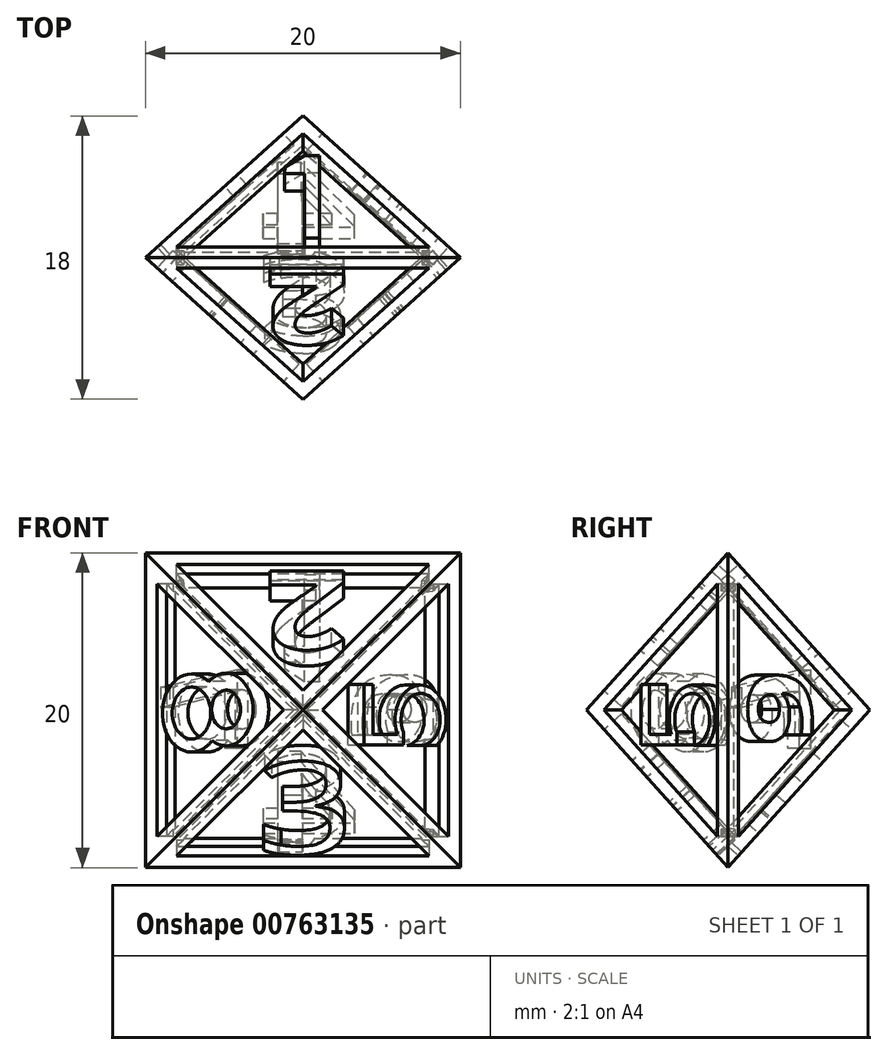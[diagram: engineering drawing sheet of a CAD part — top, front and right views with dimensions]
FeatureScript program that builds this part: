
annotation { "Feature Type Name" : "Feature", "Feature Type Description" : "" }
export const myFeature = defineFeature(function(context is Context, id is Id, definition is map)
    precondition{}
    {
        {
            var Q0;
            Q0=qCreatedBy(makeId("Front.planeOp"),FACE);
            var sketch = newSketch(context, id + "F0", { "sketchPlane" : qUnion([Q0])});
            skLineSegment(sketch, "E0.bottom", {"start": v(-18.05, 11.57) * mm, "end": v(1.95, 11.57) * mm});
            skLineSegment(sketch, "E0.top", {"start": v(-18.05, -8.43) * mm, "end": v(1.95, -8.43) * mm});
            skLineSegment(sketch, "E0.left", {"start": v(-18.05, 11.57) * mm, "end": v(-18.05, -8.43) * mm});
            skLineSegment(sketch, "E0.right", {"start": v(1.95, 11.57) * mm, "end": v(1.95, -8.43) * mm});
            skSolve(sketch);
        }
        {
            var Q0;
            Q0=makeQuery(id+"F0.imprint","IMPRINT",FACE,{"disambiguationData":[TD([[makeQuery(id+"F0.imprint","IMPRINT",EDGE,{"derivedFrom":sQuery(id+"F0.wireOp",EDGE,"E0.bottom")}),-1.0]])]});
            extrude(context, id + "F1", {"entities" : qUnion([Q0]), "depth" : 20 * mm, "offsetDistance" : 25.4 * mm, "hasDraft" : true, "draftAngle" : 48 * degree, "draftPullDirection" : true});
        }
        {
            var Q0;
            Q0=makeQuery(id+"F1.opExtrude","CAP_FACE",FACE,{"disambiguationData":[OSD([sQuery(id+"F0.wireOp",EDGE,"E0.bottom"),sQuery(id+"F0.wireOp",EDGE,"E0.top"),sQuery(id+"F0.wireOp",EDGE,"E0.left"),sQuery(id+"F0.wireOp",EDGE,"E0.right")])],"isStart":true});
            extrude(context, id + "F2", {"entities" : qUnion([Q0]), "operationType" : NewBodyOperationType.ADD, "depth" : 21.4 * mm, "offsetDistance" : 25.4 * mm, "hasDraft" : true, "draftAngle" : 48 * degree, "draftPullDirection" : true});
        }
        {
            var Q0;
            Q0=makeQuery(id+"F2.opExtrude","SWEPT_FACE",FACE,{"disambiguationData":[OSD([sQuery(id+"F0.wireOp",EDGE,"E0.bottom")])]});
            var sketch = newSketch(context, id + "F3", { "sketchPlane" : qUnion([Q0])});
            skLineSegment(sketch, "E1.0", {"start": v(8.05, -3.18) * mm, "end": v(16.06, 7.6) * mm});
            skLineSegment(sketch, "E1.1", {"start": v(8.05, -3.18) * mm, "end": v(0.04, 7.6) * mm});
            skLineSegment(sketch, "E1.2", {"start": v(16.06, 7.6) * mm, "end": v(0.04, 7.6) * mm});
            skLineSegment(sketch, "E2", {"start": v(9.21, 0.62) * mm, "end": v(7.96, 0.62) * mm});
            skLineSegment(sketch, "E3", {"start": v(7.96, 0.62) * mm, "end": v(7.96, 6.75) * mm});
            skLineSegment(sketch, "E4", {"start": v(7.96, 6.75) * mm, "end": v(7, 6.75) * mm});
            skLineSegment(sketch, "E5", {"start": v(7, 6.75) * mm, "end": v(7, -1.1) * mm});
            skLineSegment(sketch, "E6", {"start": v(7, -1.1) * mm, "end": v(7.96, -1.1) * mm});
            skLineSegment(sketch, "E7", {"start": v(7.96, -1.1) * mm, "end": v(9.2, 0) * mm});
            skLineSegment(sketch, "E8", {"start": v(9.2, 0) * mm, "end": v(9.21, 0.62) * mm});
            skSolve(sketch);
        }
        {
            var Q0;
            Q0=makeQuery(id+"F2.opExtrude","SWEPT_FACE",FACE,{"disambiguationData":[OSD([sQuery(id+"F0.wireOp",EDGE,"E0.right")])]});
            var sketch = newSketch(context, id + "F4", { "sketchPlane" : qUnion([Q0])});
            skLineSegment(sketch, "E9.0", {"start": v(10.33, 1.57) * mm, "end": v(-0.45, -6.44) * mm});
            skLineSegment(sketch, "E9.1", {"start": v(10.33, 1.57) * mm, "end": v(-0.45, 9.58) * mm});
            skLineSegment(sketch, "E9.2", {"start": v(-0.45, 9.58) * mm, "end": v(-0.45, -6.44) * mm});
            skText(sketch, "E10", { "text": "6", "fontName": "OpenSans-Bold.ttf"});
            const initialGuessF4  = {"E10": [0.0005, 0.0041, 0, -1, 0.00604]};
            skSetInitialGuess(sketch, initialGuessF4);
            skSolve(sketch);
        }
        {
            var Q0;
            Q0=makeQuery(id+"F2.opExtrude","SWEPT_FACE",FACE,{"disambiguationData":[OSD([sQuery(id+"F0.wireOp",EDGE,"E0.top")])]});
            var sketch = newSketch(context, id + "F5", { "sketchPlane" : qUnion([Q0])});
            skLineSegment(sketch, "E11.0", {"start": v(8.05, 5.52) * mm, "end": v(16.06, -5.26) * mm});
            skLineSegment(sketch, "E11.1", {"start": v(8.05, 5.52) * mm, "end": v(0.04, -5.26) * mm});
            skLineSegment(sketch, "E11.2", {"start": v(16.06, -5.26) * mm, "end": v(0.04, -5.26) * mm});
            skText(sketch, "E12", { "text": "4", "fontName": "OpenSans-Bold.ttf"});
            const initialGuessF5  = {"E12": [0.0046, -0.00494, 1, 0, 0.00776]};
            skSetInitialGuess(sketch, initialGuessF5);
            skSolve(sketch);
        }
        {
            var Q0;
            Q0=makeQuery(id+"F2.opExtrude","SWEPT_FACE",FACE,{"disambiguationData":[OSD([sQuery(id+"F0.wireOp",EDGE,"E0.left")])]});
            var sketch = newSketch(context, id + "F6", { "sketchPlane" : qUnion([Q0])});
            skLineSegment(sketch, "E13.0", {"start": v(1.63, 1.57) * mm, "end": v(12.41, -6.44) * mm});
            skLineSegment(sketch, "E13.1", {"start": v(1.63, 1.57) * mm, "end": v(12.41, 9.58) * mm});
            skLineSegment(sketch, "E13.2", {"start": v(12.41, 9.58) * mm, "end": v(12.41, -6.44) * mm});
            skLineSegment(sketch, "E14", {"start": v(5.54, -0.87) * mm, "end": v(5.54, 4.13) * mm});
            skLineSegment(sketch, "E15", {"start": v(5.54, 4.13) * mm, "end": v(12.13, 3) * mm});
            skLineSegment(sketch, "E16", {"start": v(12.13, 3) * mm, "end": v(12.13, 1.76) * mm});
            skLineSegment(sketch, "E17", {"start": v(12.13, 1.76) * mm, "end": v(6.65, 2.75) * mm});
            skLineSegment(sketch, "E18", {"start": v(6.65, 2.75) * mm, "end": v(6.65, -0.82) * mm});
            skLineSegment(sketch, "E19", {"start": v(6.65, -0.82) * mm, "end": v(5.54, -0.87) * mm});
            skSolve(sketch);
        }
        {
            var Q0;
            Q0=makeQuery(id+"F1.opExtrude","SWEPT_FACE",FACE,{"disambiguationData":[OSD([sQuery(id+"F0.wireOp",EDGE,"E0.left")])]});
            var sketch = newSketch(context, id + "F7", { "sketchPlane" : qUnion([Q0])});
            skLineSegment(sketch, "E20.0", {"start": v(-1.63, 1.57) * mm, "end": v(-12.41, 9.58) * mm});
            skLineSegment(sketch, "E20.1", {"start": v(-1.63, 1.57) * mm, "end": v(-12.41, -6.44) * mm});
            skLineSegment(sketch, "E20.2", {"start": v(-12.41, 9.58) * mm, "end": v(-12.41, -6.44) * mm});
            skCircle(sketch, "E21", {"center": v(-6.52, 1.62) * mm, "radius": 1.32 * mm});
            skCircle(sketch, "E22", {"center": v(-9.48, 1.4) * mm, "radius": 1.65 * mm});
            skArc(sketch, "E23", {"start": v(-7.72, -0.36) * mm, "mid": v(-4.23, 1.8) * mm, "end": v(-8, 3.39) * mm});
            skArc(sketch, "E24", {"start": v(-8, 3.39) * mm, "mid": v(-11.96, 1.2) * mm, "end": v(-7.72, -0.36) * mm});
            skCircle(sketch, "E25", {"center": v(-6.52, 1.62) * mm, "radius": 1.23 * mm});
            skSolve(sketch);
        }
        {
            var Q0;
            Q0=makeQuery(id+"F1.opExtrude","SWEPT_FACE",FACE,{"disambiguationData":[OSD([sQuery(id+"F0.wireOp",EDGE,"E0.bottom")])]});
            var sketch = newSketch(context, id + "F8", { "sketchPlane" : qUnion([Q0])});
            skLineSegment(sketch, "E26.0", {"start": v(-8.05, -3.18) * mm, "end": v(-0.04, 7.6) * mm});
            skLineSegment(sketch, "E26.1", {"start": v(-8.05, -3.18) * mm, "end": v(-16.06, 7.6) * mm});
            skLineSegment(sketch, "E26.2", {"start": v(-16.06, 7.6) * mm, "end": v(-0.04, 7.6) * mm});
            skText(sketch, "E27", { "text": "2", "fontName": "OpenSans-Bold.ttf"});
            const initialGuessF8  = {"E27": [-0.0051, 0.00702, -1, 0, 0.00672]};
            skSetInitialGuess(sketch, initialGuessF8);
            skSolve(sketch);
        }
        {
            var Q0;
            Q0=makeQuery(id+"F1.opExtrude","SWEPT_FACE",FACE,{"disambiguationData":[OSD([sQuery(id+"F0.wireOp",EDGE,"E0.right")])]});
            var sketch = newSketch(context, id + "F9", { "sketchPlane" : qUnion([Q0])});
            skLineSegment(sketch, "E28.0", {"start": v(-10.33, 1.57) * mm, "end": v(0.45, -6.44) * mm});
            skLineSegment(sketch, "E28.1", {"start": v(-10.33, 1.57) * mm, "end": v(0.45, 9.58) * mm});
            skLineSegment(sketch, "E28.2", {"start": v(0.45, 9.58) * mm, "end": v(0.45, -6.44) * mm});
            skLineSegment(sketch, "E29", {"start": v(-6.8, 3.2) * mm, "end": v(-6.01, 3.2) * mm});
            skLineSegment(sketch, "E30", {"start": v(-6.01, 3.2) * mm, "end": v(-6.01, 0.03) * mm});
            skLineSegment(sketch, "E31", {"start": v(-6.01, 0.03) * mm, "end": v(-3.91, 0.03) * mm});
            skLineSegment(sketch, "E32", {"start": v(-3.68, -0.62) * mm, "end": v(-6.8, -0.62) * mm});
            skLineSegment(sketch, "E33", {"start": v(-6.8, -0.62) * mm, "end": v(-6.8, 3.2) * mm});
            skArc(sketch, "E34", {"start": v(-0.52, -0.67) * mm, "mid": v(-1.5, 3.12) * mm, "end": v(-3.91, 0.03) * mm});
            skLineSegment(sketch, "E35", {"start": v(-0.52, -0.67) * mm, "end": v(-1.77, -0.67) * mm});
            skArc(sketch, "E36", {"start": v(-1.77, -0.67) * mm, "mid": v(-1.18, 2.45) * mm, "end": v(-3.4, 0.19) * mm});
            skLineSegment(sketch, "E37", {"start": v(-3.68, -0.62) * mm, "end": v(-3.4, -0.63) * mm});
            skLineSegment(sketch, "E38", {"start": v(-3.4, -0.63) * mm, "end": v(-3.4, 0.19) * mm});
            skSolve(sketch);
        }
        {
            var Q0;
            Q0=makeQuery(id+"F1.opExtrude","SWEPT_FACE",FACE,{"disambiguationData":[OSD([sQuery(id+"F0.wireOp",EDGE,"E0.top")])]});
            var sketch = newSketch(context, id + "F10", { "sketchPlane" : qUnion([Q0])});
            skLineSegment(sketch, "E39.0", {"start": v(-8.05, 5.52) * mm, "end": v(-0.04, -5.26) * mm});
            skLineSegment(sketch, "E39.1", {"start": v(-8.05, 5.52) * mm, "end": v(-16.06, -5.26) * mm});
            skLineSegment(sketch, "E39.2", {"start": v(-16.06, -5.26) * mm, "end": v(-0.04, -5.26) * mm});
            skText(sketch, "E40", { "text": "3", "fontName": "OpenSans-Regular.ttf"});
            const initialGuessF10  = {"E40": [-0.01104, -0.0051, 1, 0, 0.0079]};
            skSetInitialGuess(sketch, initialGuessF10);
            skSolve(sketch);
        }
        {
            var Q0;
            Q0=makeQuery(id+"F8.imprint","IMPRINT",FACE,{"disambiguationData":[TD([[makeQuery(id+"F8.imprint","IMPRINT",EDGE,{"derivedFrom":sQuery(id+"F8.wireOp",EDGE,"E26.0")}),1.0]])]});
            extrude(context, id + "F11", {"entities" : qUnion([Q0]), "operationType" : NewBodyOperationType.REMOVE, "oppositeDirection" : true, "depth" : 1.5 * mm, "offsetDistance" : 25.4 * mm});
        }
        {
            var Q0;
            Q0=makeQuery(id+"F9.imprint","IMPRINT",FACE,{"disambiguationData":[TD([[makeQuery(id+"F9.imprint","IMPRINT",EDGE,{"derivedFrom":sQuery(id+"F9.wireOp",EDGE,"E28.0")}),1.0]])]});
            extrude(context, id + "F12", {"entities" : qUnion([Q0]), "operationType" : NewBodyOperationType.REMOVE, "oppositeDirection" : true, "depth" : 1.5 * mm, "offsetDistance" : 25.4 * mm});
        }
        {
            var Q0;
            Q0=makeQuery(id+"F10.imprint","IMPRINT",FACE,{"disambiguationData":[TD([[makeQuery(id+"F10.imprint","IMPRINT",EDGE,{"derivedFrom":sQuery(id+"F10.wireOp",EDGE,"E39.0")}),-1.0]])]});
            extrude(context, id + "F13", {"entities" : qUnion([Q0]), "operationType" : NewBodyOperationType.REMOVE, "oppositeDirection" : true, "depth" : 1.5 * mm, "offsetDistance" : 25.4 * mm});
        }
        {
            var Q0;
            Q0=makeQuery(id+"F7.imprint","IMPRINT",FACE,{"disambiguationData":[TD([[makeQuery(id+"F7.imprint","IMPRINT",EDGE,{"derivedFrom":sQuery(id+"F7.wireOp",EDGE,"E20.0")}),1.0]])]});
            var Q1;
            Q1=makeQuery(id+"F7.imprint","IMPRINT",FACE,{"disambiguationData":[TD([[makeQuery(id+"F7.imprint","IMPRINT",EDGE,{"derivedFrom":sQuery(id+"F7.wireOp",EDGE,"E22")}),1.0]])]});
            extrude(context, id + "F14", {"entities" : qUnion([Q0, Q1]), "operationType" : NewBodyOperationType.REMOVE, "oppositeDirection" : true, "depth" : 1.5 * mm, "offsetDistance" : 25.4 * mm});
        }
        {
            var Q0;
            Q0=makeQuery(id+"F7.imprint","IMPRINT",FACE,{"disambiguationData":[TD([[makeQuery(id+"F7.imprint","IMPRINT",EDGE,{"derivedFrom":sQuery(id+"F7.wireOp",EDGE,"E25")}),1.0]])]});
            extrude(context, id + "F15", {"entities" : qUnion([Q0]), "operationType" : NewBodyOperationType.REMOVE, "oppositeDirection" : true, "depth" : 1.5 * mm, "offsetDistance" : 25.4 * mm});
        }
        {
            var Q0;
            Q0=makeQuery(id+"F4.imprint","IMPRINT",FACE,{"disambiguationData":[TD([[makeQuery(id+"F4.imprint","IMPRINT",EDGE,{"derivedFrom":sQuery(id+"F4.wireOp",EDGE,"E9.0")}),-1.0]])]});
            var Q1;
            Q1=makeQuery(id+"F4.imprint","IMPRINT",FACE,{"disambiguationData":[TD([[makeQuery(id+"F4.imprint","IMPRINT",EDGE,{"derivedFrom":sQuery(id+"F4.wireOp",EDGE,"dba62e90-3ad5-415a-88f1-9e4a70c25716")}),1.0]])]});
            var Q2;
            Q2=makeQuery(id+"F4.imprint","IMPRINT",FACE,{"disambiguationData":[TD([[makeQuery(id+"F4.imprint","IMPRINT",EDGE,{"derivedFrom":sQuery(id+"F4.wireOp",EDGE,"E10.sketch_text.stroke-17")}),1.0]])]});
            extrude(context, id + "F16", {"entities" : qUnion([Q0, Q1, Q2]), "operationType" : NewBodyOperationType.REMOVE, "oppositeDirection" : true, "depth" : 1.5 * mm, "offsetDistance" : 25.4 * mm});
        }
        {
            var Q0;
            Q0=makeQuery(id+"F3.imprint","IMPRINT",FACE,{"disambiguationData":[TD([[makeQuery(id+"F3.imprint","IMPRINT",EDGE,{"derivedFrom":sQuery(id+"F3.wireOp",EDGE,"E1.0")}),1.0]])]});
            extrude(context, id + "F17", {"entities" : qUnion([Q0]), "operationType" : NewBodyOperationType.REMOVE, "oppositeDirection" : true, "depth" : 1.5 * mm, "offsetDistance" : 25.4 * mm});
        }
        {
            var Q0;
            Q0=makeQuery(id+"F6.imprint","IMPRINT",FACE,{"disambiguationData":[TD([[makeQuery(id+"F6.imprint","IMPRINT",EDGE,{"derivedFrom":sQuery(id+"F6.wireOp",EDGE,"E13.0")}),1.0]])]});
            extrude(context, id + "F18", {"entities" : qUnion([Q0]), "operationType" : NewBodyOperationType.REMOVE, "oppositeDirection" : true, "depth" : 1 * mm, "offsetDistance" : 25.4 * mm});
        }
        {
            var Q0;
            Q0=makeQuery(id+"F5.imprint","IMPRINT",FACE,{"disambiguationData":[TD([[makeQuery(id+"F5.imprint","IMPRINT",EDGE,{"derivedFrom":sQuery(id+"F5.wireOp",EDGE,"E11.0")}),-1.0]])]});
            var Q1;
            Q1=makeQuery(id+"F5.imprint","IMPRINT",FACE,{"disambiguationData":[TD([[makeQuery(id+"F5.imprint","IMPRINT",EDGE,{"derivedFrom":sQuery(id+"F5.wireOp",EDGE,"E12.sketch_text.stroke-11")}),1.0]])]});
            extrude(context, id + "F19", {"entities" : qUnion([Q0, Q1]), "operationType" : NewBodyOperationType.REMOVE, "oppositeDirection" : true, "depth" : 1 * mm, "offsetDistance" : 25.4 * mm});
        }
    });
